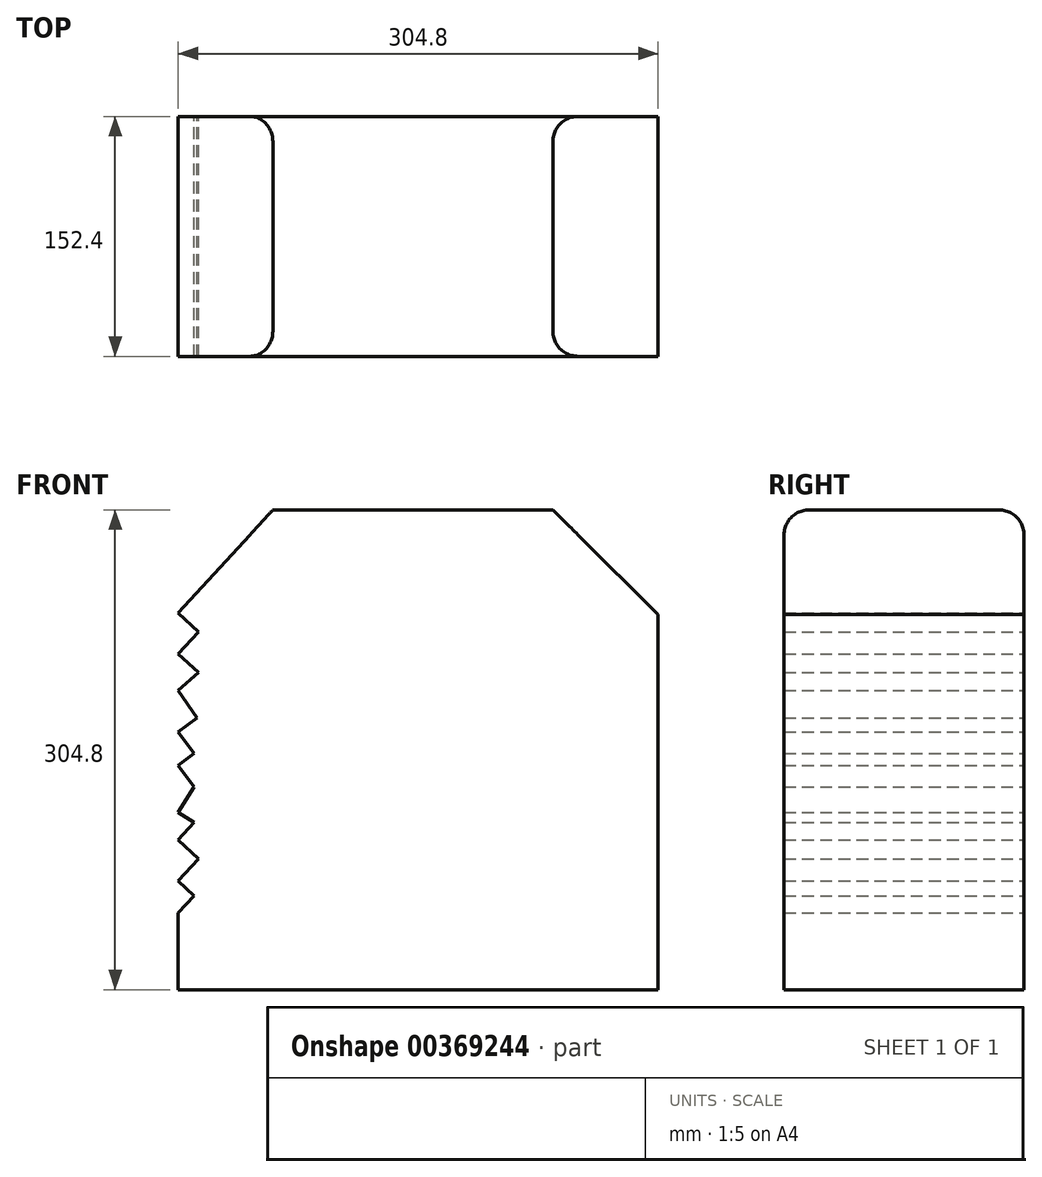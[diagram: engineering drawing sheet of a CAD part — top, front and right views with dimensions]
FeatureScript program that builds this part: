
annotation { "Feature Type Name" : "Feature", "Feature Type Description" : "" }
export const myFeature = defineFeature(function(context is Context, id is Id, definition is map)
    precondition{}
    {
        {
            var Q0;
            Q0=qCreatedBy(makeId("Front.planeOp"),FACE);
            var sketch = newSketch(context, id + "F0", { "sketchPlane" : qUnion([Q0])});
            skLineSegment(sketch, "E0.top", {"start": v(-233.71, -149.95) * mm, "end": v(71.09, -149.95) * mm});
            skLineSegment(sketch, "E0.right", {"start": v(71.09, 44.35) * mm, "end": v(71.09, -149.95) * mm});
            skLineSegment(sketch, "E1", {"start": v(-233.71, 89.22) * mm, "end": v(-173.58, 154.85) * mm});
            skLineSegment(sketch, "E2", {"start": v(-173.58, 154.85) * mm, "end": v(4.22, 154.85) * mm});
            skLineSegment(sketch, "E3", {"start": v(4.22, 154.85) * mm, "end": v(71.09, 88.53) * mm});
            skLineSegment(sketch, "E4", {"start": v(71.09, 88.53) * mm, "end": v(71.09, 44.35) * mm});
            skLineSegment(sketch, "E5", {"start": v(-233.71, 89.22) * mm, "end": v(-220.78, 77.37) * mm});
            skLineSegment(sketch, "E6", {"start": v(-220.78, 77.37) * mm, "end": v(-233.71, 63.25) * mm});
            skLineSegment(sketch, "E7", {"start": v(-233.71, 63.25) * mm, "end": v(-220.78, 51.4) * mm});
            skLineSegment(sketch, "E8", {"start": v(-220.78, 51.4) * mm, "end": v(-233.71, 40.2) * mm});
            skLineSegment(sketch, "E9", {"start": v(-220.78, 22.75) * mm, "end": v(-233.71, 13.76) * mm});
            skLineSegment(sketch, "E10", {"start": v(-233.71, 13.76) * mm, "end": v(-220.78, 22.75) * mm});
            skLineSegment(sketch, "E11", {"start": v(-233.71, 40.2) * mm, "end": v(-221.58, 22.75) * mm});
            skLineSegment(sketch, "E12", {"start": v(-221.58, 22.75) * mm, "end": v(-233.71, 13.76) * mm});
            skLineSegment(sketch, "E13", {"start": v(-233.71, 13.76) * mm, "end": v(-223.52, 0) * mm});
            skLineSegment(sketch, "E14", {"start": v(-223.52, 0) * mm, "end": v(-233.71, -7.55) * mm});
            skLineSegment(sketch, "E15", {"start": v(-233.71, -7.55) * mm, "end": v(-223.52, -21.32) * mm});
            skLineSegment(sketch, "E16", {"start": v(-223.52, -21.32) * mm, "end": v(-233.71, -37.35) * mm});
            skLineSegment(sketch, "E17", {"start": v(-233.71, -37.35) * mm, "end": v(-223.52, -43.83) * mm});
            skLineSegment(sketch, "E18", {"start": v(-223.52, -43.83) * mm, "end": v(-233.71, -54.87) * mm});
            skLineSegment(sketch, "E19", {"start": v(-233.71, -54.87) * mm, "end": v(-220.78, -66.82) * mm});
            skLineSegment(sketch, "E20", {"start": v(-220.78, -66.82) * mm, "end": v(-233.71, -80.82) * mm});
            skLineSegment(sketch, "E21", {"start": v(-233.71, -80.82) * mm, "end": v(-223.52, -90.24) * mm});
            skLineSegment(sketch, "E22", {"start": v(-223.52, -90.24) * mm, "end": v(-233.71, -101.27) * mm});
            skLineSegment(sketch, "E23.trimOffspring", {"start": v(-233.71, -101.27) * mm, "end": v(-233.71, -149.95) * mm});
            skSolve(sketch);
        }
        {
            var Q0;
            Q0 = qSketchRegion(id + "F0", true);
            extrude(context, id + "F1", {"entities" : qUnion([Q0]), "depth" : 152.4 * mm});
        }
        {
            var Q0;
            Q0=makeQuery(id+"F1.opExtrude","CAP_EDGE",EDGE,{"disambiguationData":[OSD([sQuery(id+"F0.wireOp",EDGE,"CsNU8bbd-MdnX-a1Q9-r08P-Skj0sF4IjyNM")])],"isStart":true});
            var Q1;
            Q1=makeQuery(id+"F1.opExtrude","SWEPT_EDGE",EDGE,{"disambiguationData":[OSD([sQuery(id+"F0.wireOp",EDGE,"Zz107JAa-y22P-XzNK-cATG-PG1s2mre6aBR"),sQuery(id+"F0.wireOp",EDGE,"CsNU8bbd-MdnX-a1Q9-r08P-Skj0sF4IjyNM")])]});
            var Q2;
            Q2=makeQuery(id+"F1.opExtrude","CAP_EDGE",EDGE,{"disambiguationData":[OSD([sQuery(id+"F0.wireOp",EDGE,"E2")])],"isStart":false});
            var Q3;
            Q3=makeQuery(id+"F1.opExtrude","CAP_EDGE",EDGE,{"disambiguationData":[OSD([sQuery(id+"F0.wireOp",EDGE,"E2")])],"isStart":true});
            fillet(context, id + "F2", {"entities" : qUnion([Q0, Q1, Q2, Q3]), "radius" : 15.94 * mm, "tangentPropagation" : true, "allowEdgeOverflow" : false});
        }
    });
